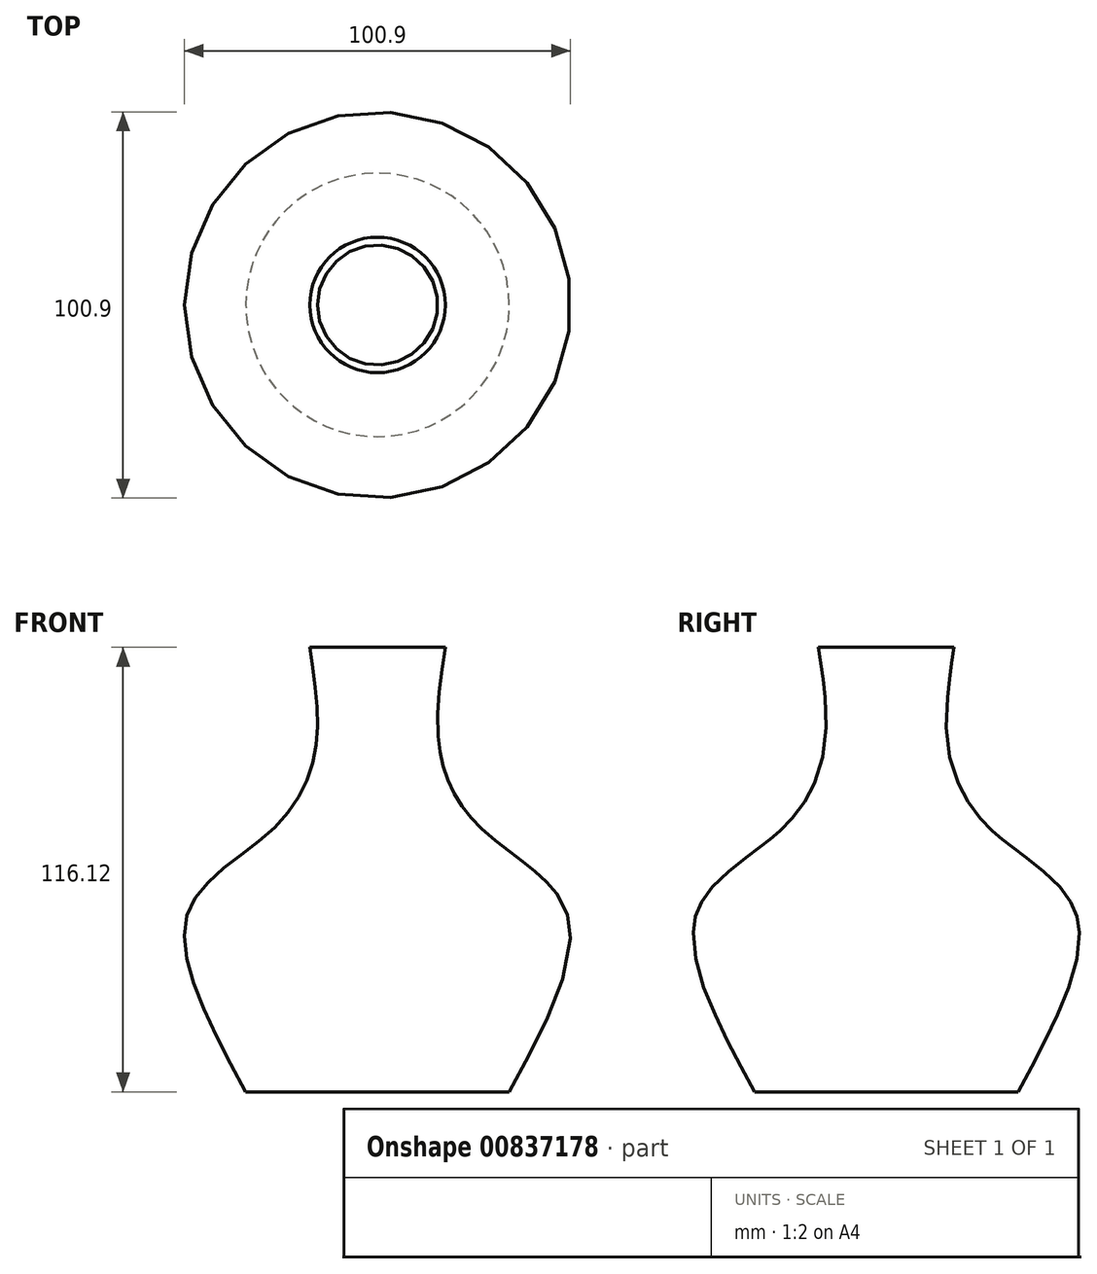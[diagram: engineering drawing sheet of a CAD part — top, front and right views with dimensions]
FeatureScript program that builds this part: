
annotation { "Feature Type Name" : "Feature", "Feature Type Description" : "" }
export const myFeature = defineFeature(function(context is Context, id is Id, definition is map)
    precondition{}
    {
        {
            var Q0;
            Q0=qCreatedBy(makeId("Right.planeOp"),FACE);
            var sketch = newSketch(context, id + "F0", { "sketchPlane" : qUnion([Q0])});
            skFitSpline(sketch, "E0", {"points": [v(17.7, 48.06) * mm, v(16.23, 21.27) * mm, v(27.9, 0) * mm, v(49.61, -21.52) * mm, v(34.4, -68.06) * mm], "startDerivative": vector(-18.36, -120.72) * mm, "endDerivative": vector(-92, -169.52) * mm});
            skSolve(sketch);
        }
        {
            var Q0;
            Q0=qCreatedBy(makeId("Right.planeOp"),FACE);
            var sketch = newSketch(context, id + "F1", { "sketchPlane" : qUnion([Q0])});
            skLineSegment(sketch, "E1", {"start": v(0, 62.4) * mm, "end": v(0, -68.6) * mm});
            skSolve(sketch);
        }
        {
            var Q0;
            Q0=sQuery(id+"F0.wireOp",EDGE,"E0");
            var Q1;
            Q1=sQuery(id+"F1.wireOp",EDGE,"E1");
            revolve(context, id + "F2", {"bodyType" : ToolBodyType.SURFACE, "surfaceOperationType" : NewSurfaceOperationType.NEW, "surfaceEntities" : qUnion([Q0]), "axis" : qUnion([Q1]), "revolveType" : RevolveType.FULL});
        }
    });
